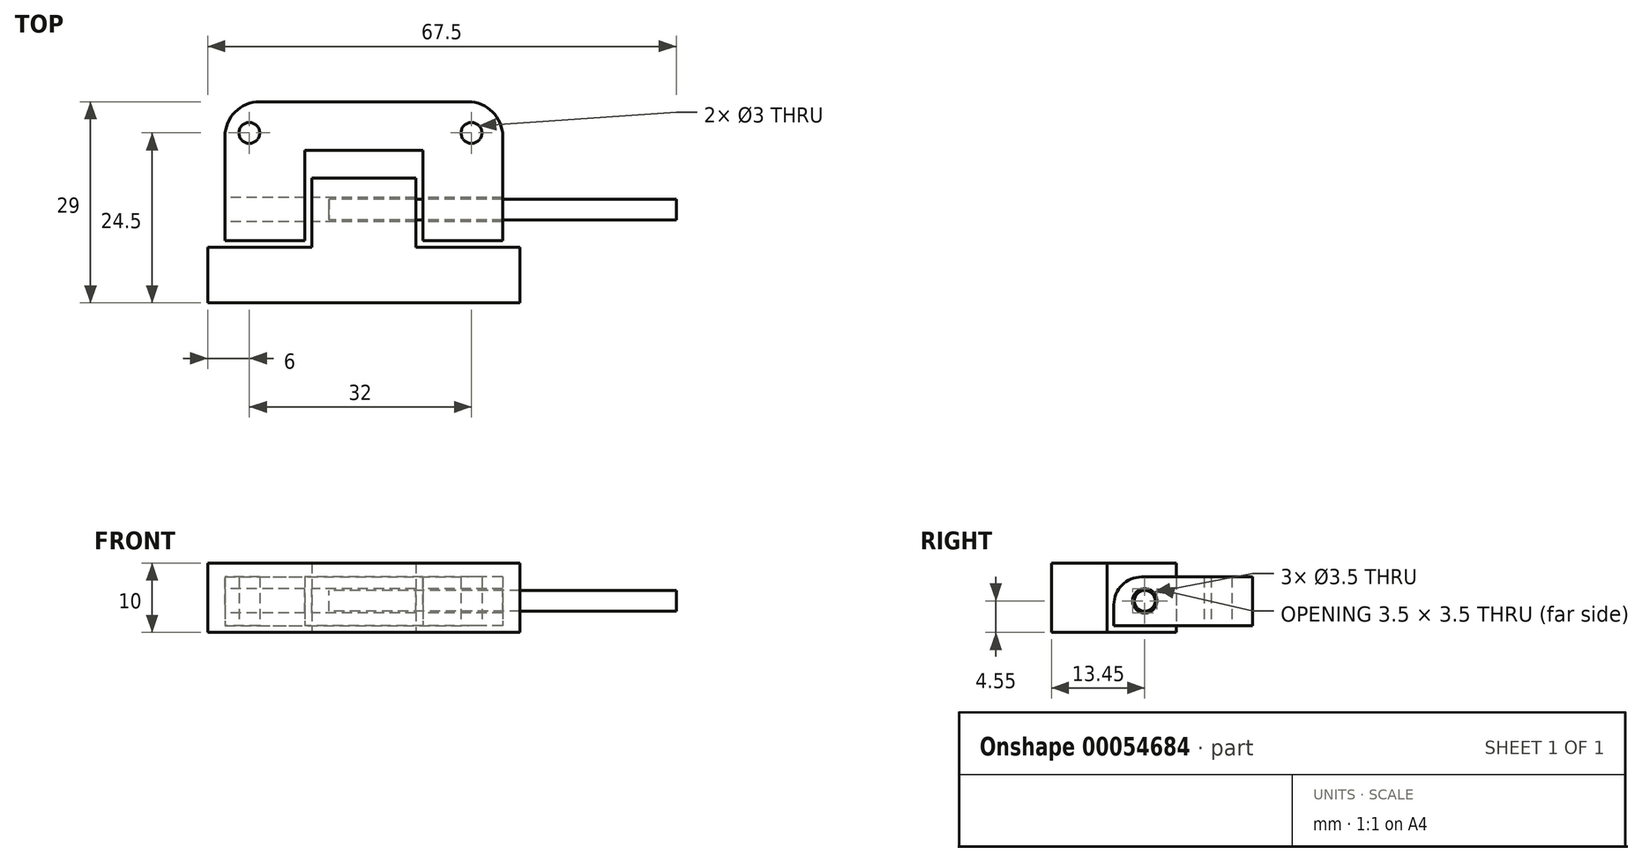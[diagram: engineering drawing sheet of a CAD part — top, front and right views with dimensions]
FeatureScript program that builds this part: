
annotation { "Feature Type Name" : "Feature", "Feature Type Description" : "" }
export const myFeature = defineFeature(function(context is Context, id is Id, definition is map)
    precondition{}
    {
        {
            var Q0;
            Q0=qCreatedBy(makeId("Top.planeOp"),FACE);
            var sketch = newSketch(context, id + "F0", { "sketchPlane" : qUnion([Q0])});
            skLineSegment(sketch, "E0.bottom", {"start": v(0, 0) * mm, "end": v(15, 0) * mm});
            skLineSegment(sketch, "E0.left", {"start": v(0, 0) * mm, "end": v(0, -10) * mm});
            skLineSegment(sketch, "E0.right", {"start": v(15, 0) * mm, "end": v(15, -10) * mm});
            skLineSegment(sketch, "E1.top", {"start": v(-15, -18) * mm, "end": v(30, -18) * mm});
            skLineSegment(sketch, "E1.left", {"start": v(-15, -10) * mm, "end": v(-15, -18) * mm});
            skLineSegment(sketch, "E1.right", {"start": v(30, -10) * mm, "end": v(30, -18) * mm});
            skLineSegment(sketch, "E2", {"start": v(-15, -10) * mm, "end": v(0, -10) * mm});
            skLineSegment(sketch, "E3", {"start": v(15, -10) * mm, "end": v(30, -10) * mm});
            skLineSegment(sketch, "E4.bottom", {"start": v(-12.5, -9) * mm, "end": v(-1, -9) * mm});
            skLineSegment(sketch, "E4.left", {"start": v(-12.5, -9) * mm, "end": v(-12.5, 11) * mm});
            skLineSegment(sketch, "E5", {"start": v(-12.5, 11) * mm, "end": v(27.5, 11) * mm});
            skLineSegment(sketch, "E6", {"start": v(27.5, 11) * mm, "end": v(27.5, -9) * mm});
            skLineSegment(sketch, "E7", {"start": v(27.5, -9) * mm, "end": v(16, -9) * mm});
            skLineSegment(sketch, "E8", {"start": v(16, -9) * mm, "end": v(16, 4) * mm});
            skLineSegment(sketch, "E9", {"start": v(16, 4) * mm, "end": v(-1, 4) * mm});
            skLineSegment(sketch, "E10", {"start": v(-1, 4) * mm, "end": v(-1, -9) * mm});
            skCircle(sketch, "E11", {"center": v(23, 6.5) * mm, "radius": 1.5 * mm});
            skCircle(sketch, "E12", {"center": v(-9, 6.5) * mm, "radius": 1.5 * mm});
            skSolve(sketch);
        }
        {
            var Q0;
            Q0=makeQuery(id+"F0.imprint","IMPRINT",FACE,{"disambiguationData":[TD([[makeQuery(id+"F0.imprint","IMPRINT",EDGE,{"derivedFrom":sQuery(id+"F0.wireOp",EDGE,"E0.bottom")}),-1.0]])]});
            extrude(context, id + "F1", {"entities" : qUnion([Q0]), "depth" : 10 * mm});
        }
        {
            var Q0;
            Q0=makeQuery(id+"F0.imprint","IMPRINT",FACE,{"disambiguationData":[TD([[makeQuery(id+"F0.imprint","IMPRINT",EDGE,{"derivedFrom":sQuery(id+"F0.wireOp",EDGE,"E4.bottom")}),1.0]])]});
            extrude(context, id + "F2", {"entities" : qUnion([Q0]), "depth" : 8 * mm});
        }
        {
            var Q0;
            Q0=makeQuery(id+"F1.opExtrude","SWEPT_FACE",FACE,{"disambiguationData":[OSD([sQuery(id+"F0.wireOp",EDGE,"E0.left")])]});
            var sketch = newSketch(context, id + "F3", { "sketchPlane" : qUnion([Q0])});
            skCircle(sketch, "E13", {"center": v(4.55, 4.55) * mm, "radius": 1.75 * mm});
            skSolve(sketch);
        }
        {
            var Q0;
            Q0 = qSketchRegion(id + "F3", true);
            extrude(context, id + "F4", {"entities" : qUnion([Q0]), "operationType" : NewBodyOperationType.REMOVE, "endBound" : BoundingType.SYMMETRIC, "oppositeDirection" : true, "depth" : 100 * mm});
        }
        {
            var Q0;
            Q0=makeQuery(id+"F2.opExtrude","SWEPT_FACE",FACE,{"disambiguationData":[OSD([sQuery(id+"F0.wireOp",EDGE,"E6")])]});
            var sketch = newSketch(context, id + "F5", { "sketchPlane" : qUnion([Q0])});
            skCircle(sketch, "E14", {"center": v(-4.55, 4.55) * mm, "radius": 1.5 * mm});
            skSolve(sketch);
        }
        {
            var Q0;
            Q0 = qSketchRegion(id + "F5", true);
            extrude(context, id + "F6", {"entities" : qUnion([Q0]), "endBound" : BoundingType.SYMMETRIC, "depth" : 50 * mm});
        }
        {
            var Q0;
            Q0=makeQuery(id+"F0.imprint","IMPRINT",FACE,{"disambiguationData":[TD([[makeQuery(id+"F0.imprint","IMPRINT",EDGE,{"derivedFrom":sQuery(id+"F0.wireOp",EDGE,"E4.bottom")}),1.0]])]});
            extrude(context, id + "F7", {"entities" : qUnion([Q0]), "operationType" : NewBodyOperationType.REMOVE, "depth" : 1 * mm});
        }
        {
            var Q0;
            Q0=makeQuery(id+"F2.opExtrude","CAP_EDGE",EDGE,{"disambiguationData":[OSD([sQuery(id+"F0.wireOp",EDGE,"E7")])],"isStart":false});
            var Q1;
            Q1=makeQuery(id+"F2.opExtrude","CAP_EDGE",EDGE,{"disambiguationData":[OSD([sQuery(id+"F0.wireOp",EDGE,"E4.bottom")])],"isStart":false});
            fillet(context, id + "F8", {"entities" : qUnion([Q0, Q1]), "radius" : 4 * mm, "tangentPropagation" : true, "allowEdgeOverflow" : false});
        }
        {
            var Q0;
            Q0=makeQuery(id+"F2.opExtrude","SWEPT_EDGE",EDGE,{"disambiguationData":[OSD([sQuery(id+"F0.wireOp",EDGE,"E5"),sQuery(id+"F0.wireOp",EDGE,"E6")])]});
            var Q1;
            Q1=makeQuery(id+"F2.opExtrude","SWEPT_EDGE",EDGE,{"disambiguationData":[OSD([sQuery(id+"F0.wireOp",EDGE,"E4.left"),sQuery(id+"F0.wireOp",EDGE,"E5")])]});
            fillet(context, id + "F9", {"entities" : qUnion([Q0, Q1]), "radius" : 5 * mm, "tangentPropagation" : true, "allowEdgeOverflow" : false});
        }
    });
